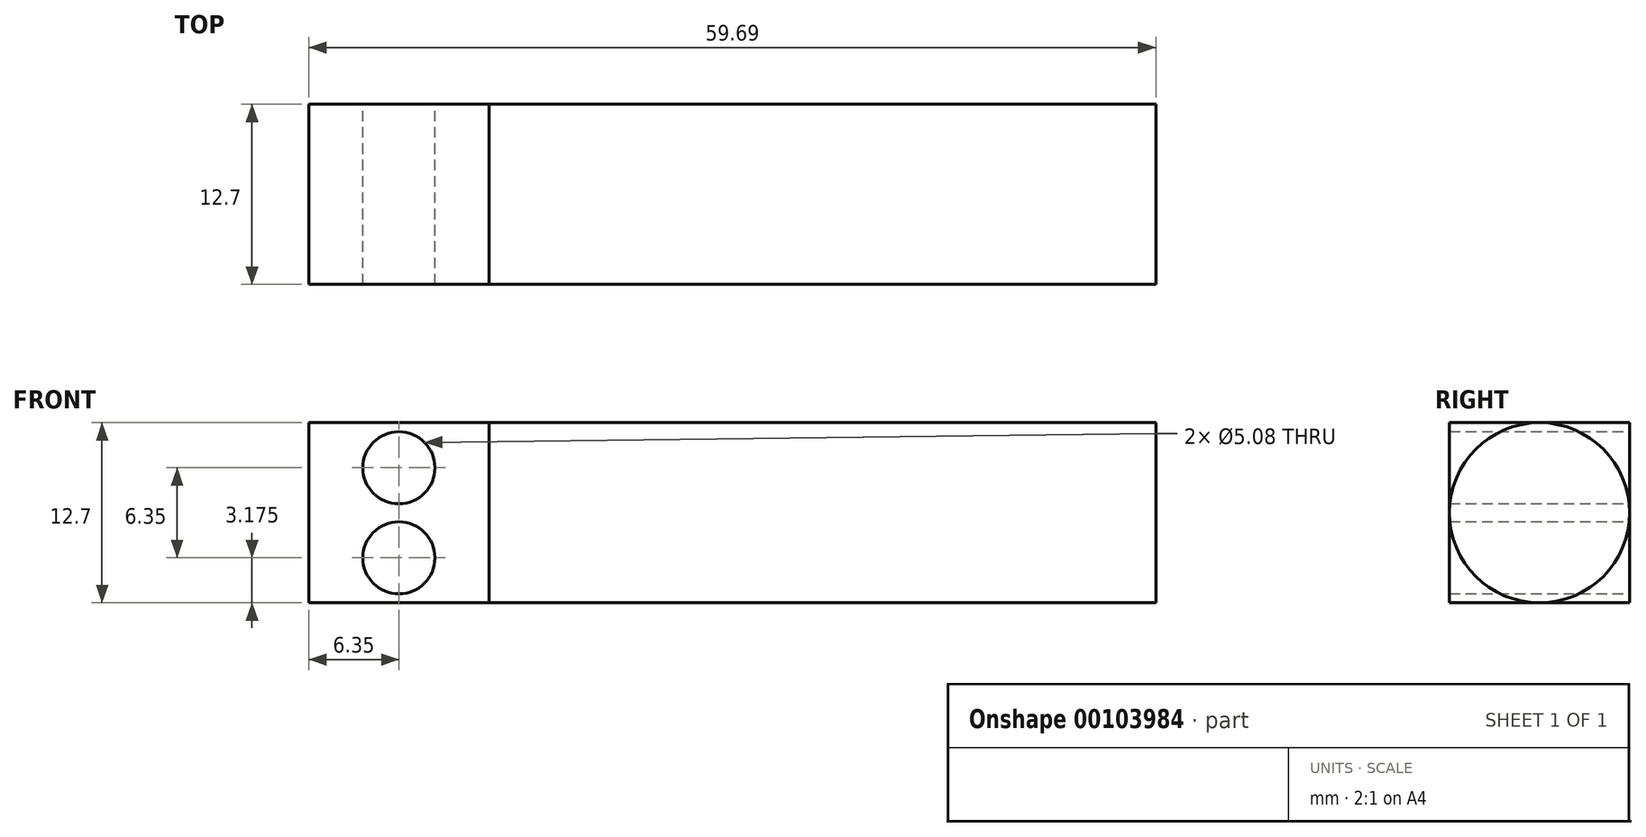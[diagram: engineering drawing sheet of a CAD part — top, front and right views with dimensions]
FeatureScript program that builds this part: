
annotation { "Feature Type Name" : "Feature", "Feature Type Description" : "" }
export const myFeature = defineFeature(function(context is Context, id is Id, definition is map)
    precondition{}
    {
        {
            var Q0;
            Q0=qCreatedBy(makeId("Right.planeOp"),FACE);
            var sketch = newSketch(context, id + "F0", { "sketchPlane" : qUnion([Q0])});
            skCircle(sketch, "E0", {"center": v(42.26, 52.7) * mm, "radius": 6.35 * mm});
            skSolve(sketch);
        }
        {
            var Q0;
            Q0 = qSketchRegion(id + "F0", true);
            extrude(context, id + "F1", {"entities" : qUnion([Q0]), "depth" : 47 * mm});
        }
        {
            var Q0;
            Q0=makeQuery(id+"F1.opExtrude","CAP_FACE",FACE,{"disambiguationData":[OSD([sQuery(id+"F0.wireOp",EDGE,"E0")])],"isStart":true});
            var sketch = newSketch(context, id + "F2", { "sketchPlane" : qUnion([Q0])});
            skLineSegment(sketch, "E1", {"start": v(-42.26, 52.7) * mm, "end": v(-48.6, 52.7) * mm, "construction": true});
            skLineSegment(sketch, "E2", {"start": v(-42.26, 52.7) * mm, "end": v(-42.26, 59.04) * mm, "construction": true});
            skLineSegment(sketch, "E3.bottom", {"start": v(-48.6, 59.04) * mm, "end": v(-35.9, 59.04) * mm});
            skLineSegment(sketch, "E3.top", {"start": v(-48.6, 46.34) * mm, "end": v(-35.9, 46.34) * mm});
            skLineSegment(sketch, "E3.left", {"start": v(-48.6, 59.04) * mm, "end": v(-48.6, 46.34) * mm});
            skLineSegment(sketch, "E3.right", {"start": v(-35.9, 59.04) * mm, "end": v(-35.9, 46.34) * mm});
            skPoint(sketch, "E3.middle", {"position": v(-42.26, 52.7) * mm});
            skSolve(sketch);
        }
        {
            var Q0;
            {var subQ0=sQuery(id+"F2.wireOp",EDGE,"E3.left");var subQ1=sQuery(id+"F2.wireOp",EDGE,"E3.bottom");var subQ2=makeQuery(id+"F2.imprint","INTERSECT",VERTEX,{"derivedFrom":[subQ1,subQ0]});Q0=makeQuery(id+"F2.imprint","IMPRINT",FACE,{"disambiguationData":[TD([[makeQuery(id+"F2.imprint","IMPRINT",EDGE,{"disambiguationData":[TD([[subQ2,-1.0]])],"derivedFrom":subQ1}),-1.0]])]});}
            var Q1;
            {var subQ0=sQuery(id+"F2.wireOp",EDGE,"E3.right");var subQ1=sQuery(id+"F2.wireOp",EDGE,"E3.bottom");var subQ2=makeQuery(id+"F2.imprint","INTERSECT",VERTEX,{"derivedFrom":[subQ1,subQ0]});Q1=makeQuery(id+"F2.imprint","IMPRINT",FACE,{"disambiguationData":[TD([[makeQuery(id+"F2.imprint","IMPRINT",EDGE,{"disambiguationData":[TD([[subQ2,1.0]])],"derivedFrom":subQ1}),-1.0]])]});}
            var Q2;
            {var subQ0=makeQuery(id+"F1.opExtrude","CAP_EDGE",EDGE,{"disambiguationData":[OSD([sQuery(id+"F0.wireOp",EDGE,"E0")])],"isStart":true});var subQ1=makeQuery(id+"F2.imprint","INTERSECT",VERTEX,{"derivedFrom":[subQ0,sQuery(id+"F2.wireOp",EDGE,"E3.bottom")]});Q2=makeQuery(id+"F2.imprint","IMPRINT",FACE,{"disambiguationData":[TD([[makeQuery(id+"F2.imprint","IMPRINT",EDGE,{"disambiguationData":[TD([[subQ1,1.0]])],"derivedFrom":subQ0}),-1.0]])]});}
            var Q3;
            {var subQ0=sQuery(id+"F2.wireOp",EDGE,"E3.left");var subQ1=sQuery(id+"F2.wireOp",EDGE,"E3.top");var subQ2=makeQuery(id+"F2.imprint","INTERSECT",VERTEX,{"derivedFrom":[subQ1,subQ0]});Q3=makeQuery(id+"F2.imprint","IMPRINT",FACE,{"disambiguationData":[TD([[makeQuery(id+"F2.imprint","IMPRINT",EDGE,{"disambiguationData":[TD([[subQ2,-1.0]])],"derivedFrom":subQ1}),1.0]])]});}
            var Q4;
            {var subQ0=sQuery(id+"F2.wireOp",EDGE,"E3.right");var subQ1=sQuery(id+"F2.wireOp",EDGE,"E3.top");var subQ2=makeQuery(id+"F2.imprint","INTERSECT",VERTEX,{"derivedFrom":[subQ1,subQ0]});Q4=makeQuery(id+"F2.imprint","IMPRINT",FACE,{"disambiguationData":[TD([[makeQuery(id+"F2.imprint","IMPRINT",EDGE,{"disambiguationData":[TD([[subQ2,1.0]])],"derivedFrom":subQ1}),1.0]])]});}
            extrude(context, id + "F3", {"entities" : qUnion([Q0, Q1, Q2, Q3, Q4]), "operationType" : NewBodyOperationType.ADD, "depth" : 12.7 * mm});
        }
        {
            var Q0;
            Q0=makeQuery(id+"F3.opExtrude","SWEPT_FACE",FACE,{"disambiguationData":[OSD([sQuery(id+"F2.wireOp",EDGE,"E3.left")])]});
            var sketch = newSketch(context, id + "F4", { "sketchPlane" : qUnion([Q0])});
            skLineSegment(sketch, "E4", {"start": v(6.35, 59.04) * mm, "end": v(6.35, 52.7) * mm});
            skPoint(sketch, "E4.endSnap0", {"position": v(12.7, 52.7) * mm});
            skLineSegment(sketch, "E5", {"start": v(6.35, 52.7) * mm, "end": v(6.35, 46.34) * mm});
            skPoint(sketch, "E6", {"position": v(6.35, 55.87) * mm});
            skPoint(sketch, "E7", {"position": v(6.35, 49.52) * mm});
            skSolve(sketch);
        }
        {
            var Q0;
            Q0=sQuery(id+"F4.wireOp",VERTEX,"E6");
            var Q1;
            Q1=sQuery(id+"F4.wireOp",VERTEX,"E7");
            var Q2;
            Q2=makeQuery(id+"F1.opExtrude","SWEPT_BODY",BODY,{"disambiguationData":[OSD([sQuery(id+"F0.wireOp",EDGE,"E0")])]});
            hole(context, id + "F5", {"style" : HoleStyle.SIMPLE, "endStyle" : HoleEndStyle.BLIND, "holeDiameter" : 5.08 * mm, "holeDepth" : 25.4 * mm, "locations" : qUnion([Q0, Q1]), "scope" : qUnion([Q2])});
        }
    });
